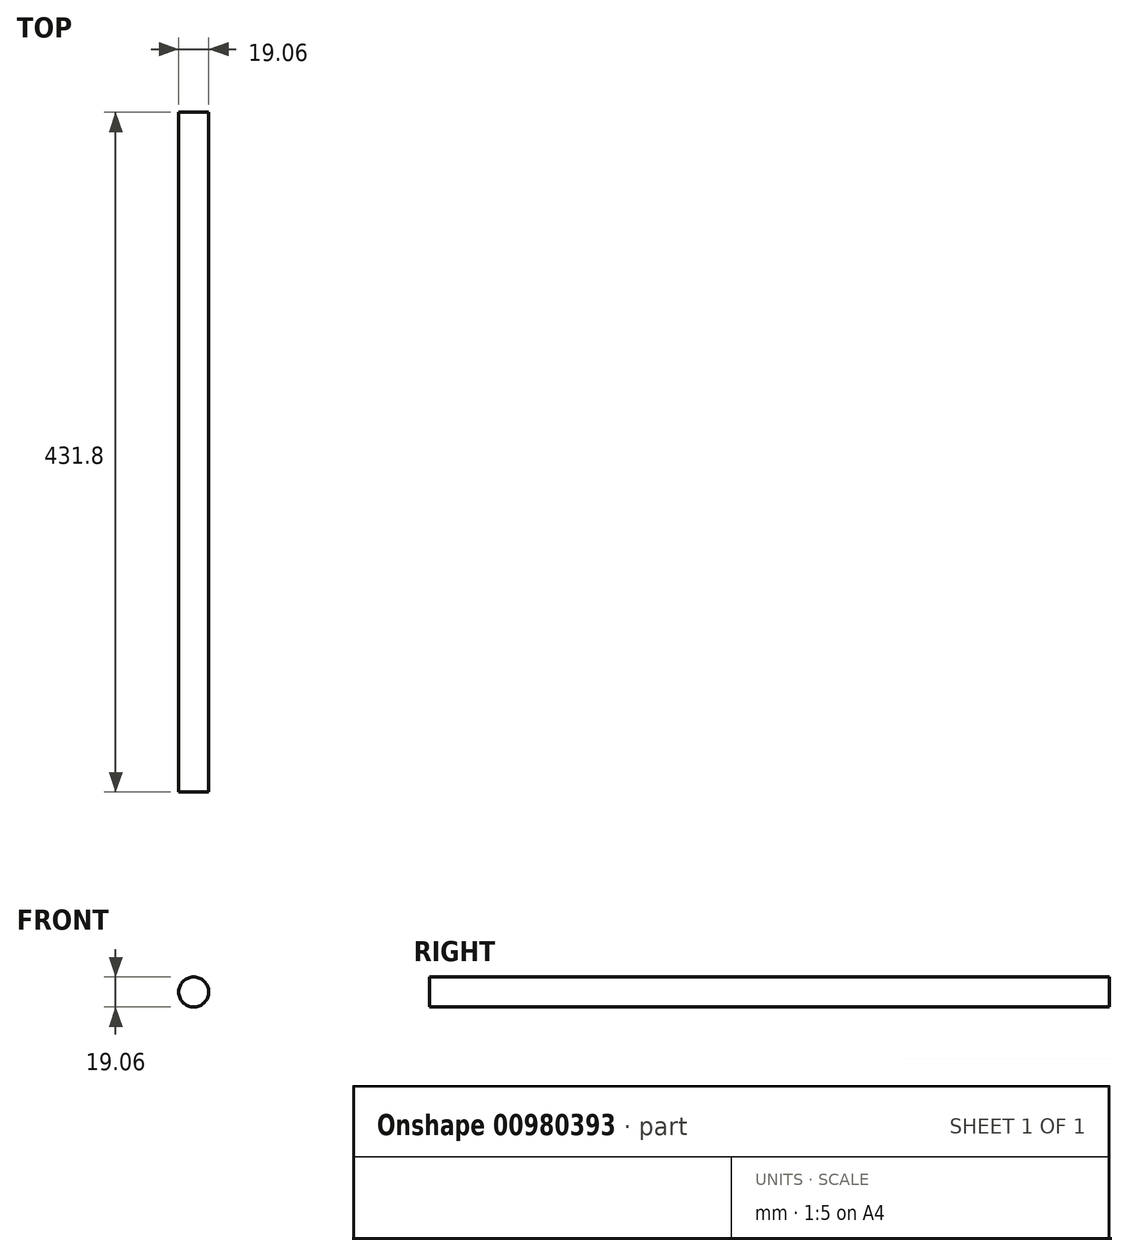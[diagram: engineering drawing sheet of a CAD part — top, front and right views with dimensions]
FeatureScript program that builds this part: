
annotation { "Feature Type Name" : "Feature", "Feature Type Description" : "" }
export const myFeature = defineFeature(function(context is Context, id is Id, definition is map)
    precondition{}
    {
        {
            var Q0;
            Q0=qCreatedBy(makeId("Front.planeOp"),FACE);
            var sketch = newSketch(context, id + "F0", { "sketchPlane" : qUnion([Q0])});
            skCircle(sketch, "E0", {"center": v(0, 0) * mm, "radius": 9.52 * mm});
            skSolve(sketch);
        }
        {
            var Q0;
            Q0 = qSketchRegion(id + "F0", true);
            extrude(context, id + "F1", {"entities" : qUnion([Q0]), "endBound" : BoundingType.SYMMETRIC, "depth" : 431.8 * mm, "offsetDistance" : 25.4 * mm});
        }
    });
